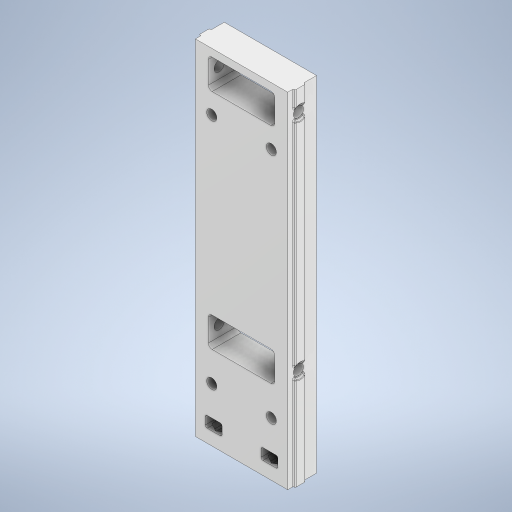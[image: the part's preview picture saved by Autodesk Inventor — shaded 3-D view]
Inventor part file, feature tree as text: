
AUTODESK INVENTOR PART (.ipt)
format: ipt  version: 2024 (Build 280153000, 153)  size: 806,912 bytes
history: native  units: mm
features: sketch x8, extrude x7, plane x5, fillet x4, hole x3, projected_geometry x3, mirror x1, chamfer x1
ambient origin geometry x8: Origin, YZ Plane, XZ Plane, XY Plane, X Axis, Y Axis, Z Axis, Center Point
bodies: Solid1 (feature_tree)
feature tree (32):
  extrude  "Extrusion1"  Depth=185.0mm
  extrude  "Extrusion2"  Depth=9.75mm
  sketch  "Sketch3"  dims[d7=1.0mm d8=5.75mm d9=0.0mm]
  plane  "Work Plane3"
  extrude  "Extrusion3"  Depth=5.75mm TaperAngle=0.0deg
  extrude  "Extrusion4"  Depth=8.25mm
  hole  "Hole1"  [1 undecoded]
  sketch  "Sketch4"  dims[d10=30.0mm d11=8.25mm]
  plane  "Work Plane4"
  extrude  "Extrusion5"  Depth=10.0mm TaperAngle=0.0deg
  fillet  "Fillet1"  Radius=7.0mm
  hole  "Hole2"  [1 undecoded]
  extrude  "Extrusion6"  Depth=10.0mm
  mirror  "Mirror1"
  chamfer  "Chamfer1"  Distance=120.0mm
  fillet  "Fillet3"  Radius=2.0mm
  fillet  "Fillet5"  Radius=6.0mm
  fillet  "Fillet6"  Radius=10.0mm
  hole  "Hole3"  [1 undecoded]
  sketch  "Sketch9"  dims[d27=-2.0mm d28=10.0mm d29=0.0mm d30=7.0mm d31=4.0mm d32=16.0mm d33=120.0mm d34=2.0mm d36=5.4mm d37=6.0mm d38=4.0mm d39=2.0mm d40=90.0deg d41=8.0mm d42=0.0mm d43=6.0mm d44=10.0mm d45=0.0mm d46=1.0mm d47=2.0mm d48=45.0deg d49=9.0mm d50=1.0mm d52=0.5mm d53=0.5mm d54=32.0mm d55=125.0mm d56=5.4mm d57=6.0mm d58=4.0mm d59=2.0mm d60=90.0deg d61=8.0mm d62=0.0mm d63=8.25mm d64=-6.0mm d65=10.0mm d66=0.0mm d67=29.0mm]
  plane  "Work Plane5"
  extrude  "Extrusion7"  Depth=10.0mm
  sketch  "Sketch1"  dims[d0=49.6mm d1=185.0mm]
  sketch  "Sketch2"  dims[d2=5.75mm d3=9.75mm d4=0.0mm d5=0.0mm d6=5.5mm]
  plane  "Work Plane1"
  plane  "Work Plane2"
  projected_geometry  "Projected Loop1"
  sketch  "Sketch5"  dims[d12=-4.0mm d13=-3.0mm d14=-6.0mm]
  sketch  "Sketch6"  dims[d15=10.0mm d16=0.0mm d17=10.0mm d18=0.0mm]
  projected_geometry  "Projected Loop2"
  sketch  "Sketch7"  dims[d19=5.4mm d20=6.0mm d21=4.0mm d22=2.0mm d23=90.0deg d24=5.0mm d25=0.0mm]
  projected_geometry  "Projected Loop5"
note: 3 required parameter values undecoded (feature->parameter linkage not recoverable at this tier; creation-order binding heuristic only, values carry confidence <= 0.55)
